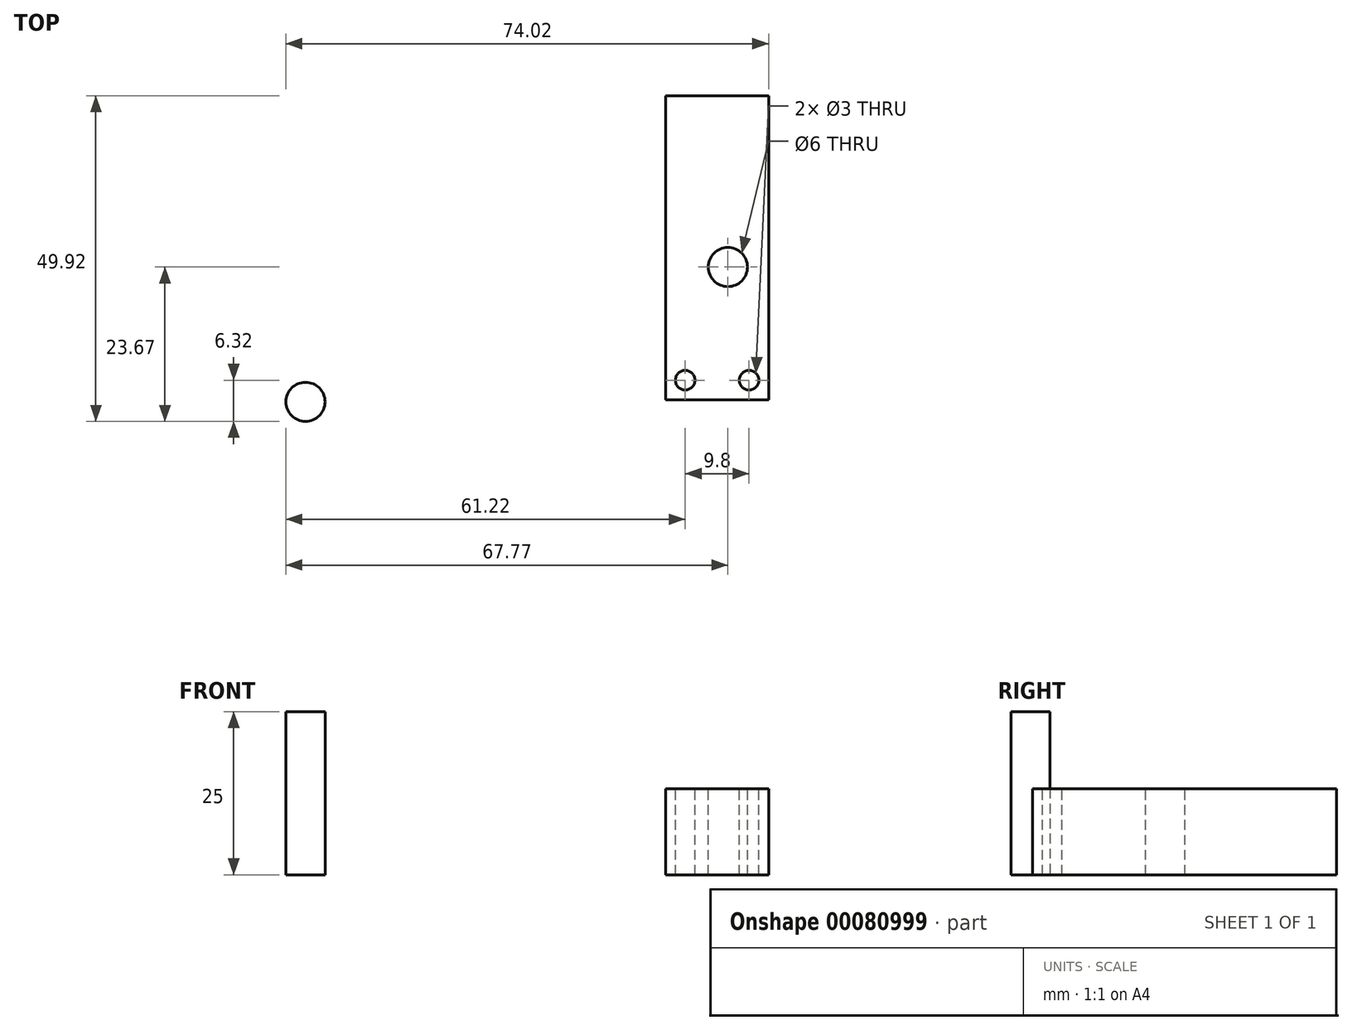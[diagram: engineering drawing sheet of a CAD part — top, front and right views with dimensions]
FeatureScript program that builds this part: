
annotation { "Feature Type Name" : "Feature", "Feature Type Description" : "" }
export const myFeature = defineFeature(function(context is Context, id is Id, definition is map)
    precondition{}
    {
        {
            var Q0;
            Q0=qCreatedBy(makeId("Top.planeOp"),FACE);
            var sketch = newSketch(context, id + "F0", { "sketchPlane" : qUnion([Q0])});
            skLineSegment(sketch, "E0.bottom", {"start": v(-7.9, 23.3) * mm, "end": v(7.9, 23.3) * mm});
            skLineSegment(sketch, "E0.top", {"start": v(-7.9, -23.3) * mm, "end": v(7.9, -23.3) * mm});
            skLineSegment(sketch, "E0.left", {"start": v(-7.9, 23.3) * mm, "end": v(-7.9, -23.3) * mm});
            skLineSegment(sketch, "E0.right", {"start": v(7.9, 23.3) * mm, "end": v(7.9, -23.3) * mm});
            skLineSegment(sketch, "E1", {"start": v(-7.9, 23.3) * mm, "end": v(7.9, -23.3) * mm, "construction": true});
            skSolve(sketch);
        }
        {
            var Q0;
            Q0=makeQuery(id+"F0.imprint","IMPRINT",FACE,{"disambiguationData":[TD([[makeQuery(id+"F0.imprint","IMPRINT",EDGE,{"derivedFrom":sQuery(id+"F0.wireOp",EDGE,"E0.bottom")}),-1.0]])]});
            extrude(context, id + "F1", {"entities" : qUnion([Q0]), "depth" : 13.2 * mm});
        }
        {
            var Q0;
            Q0=makeQuery(id+"F1.opExtrude","CAP_FACE",FACE,{"disambiguationData":[OSD([sQuery(id+"F0.wireOp",EDGE,"E0.bottom"),sQuery(id+"F0.wireOp",EDGE,"E0.top"),sQuery(id+"F0.wireOp",EDGE,"E0.left"),sQuery(id+"F0.wireOp",EDGE,"E0.right")])],"isStart":false});
            var sketch = newSketch(context, id + "F2", { "sketchPlane" : qUnion([Q0])});
            skCircle(sketch, "E2", {"center": v(1.65, -2.95) * mm, "radius": 3 * mm});
            skCircle(sketch, "E3", {"center": v(-4.9, -20.3) * mm, "radius": 1.5 * mm});
            skLineSegment(sketch, "E4", {"start": v(0, 23.3) * mm, "end": v(0, -23.3) * mm, "construction": true});
            skCircle(sketch, "E5.MirrorC", {"center": v(4.9, -20.3) * mm, "radius": 1.5 * mm});
            skSolve(sketch);
        }
        {
            var Q0;
            Q0 = qSketchRegion(id + "F2", true);
            extrude(context, id + "F3", {"entities" : qUnion([Q0]), "operationType" : NewBodyOperationType.REMOVE, "oppositeDirection" : true, "depth" : 25 * mm});
        }
        {
            var Q0;
            Q0=qCreatedBy(makeId("Top.planeOp"),FACE);
            var sketch = newSketch(context, id + "F4", { "sketchPlane" : qUnion([Q0])});
            skCircle(sketch, "E6", {"center": v(-63.12, -23.62) * mm, "radius": 3 * mm});
            skSolve(sketch);
        }
        {
            var Q0;
            Q0 = qSketchRegion(id + "F4", true);
            extrude(context, id + "F5", {"entities" : qUnion([Q0]), "depth" : 25 * mm});
        }
    });
